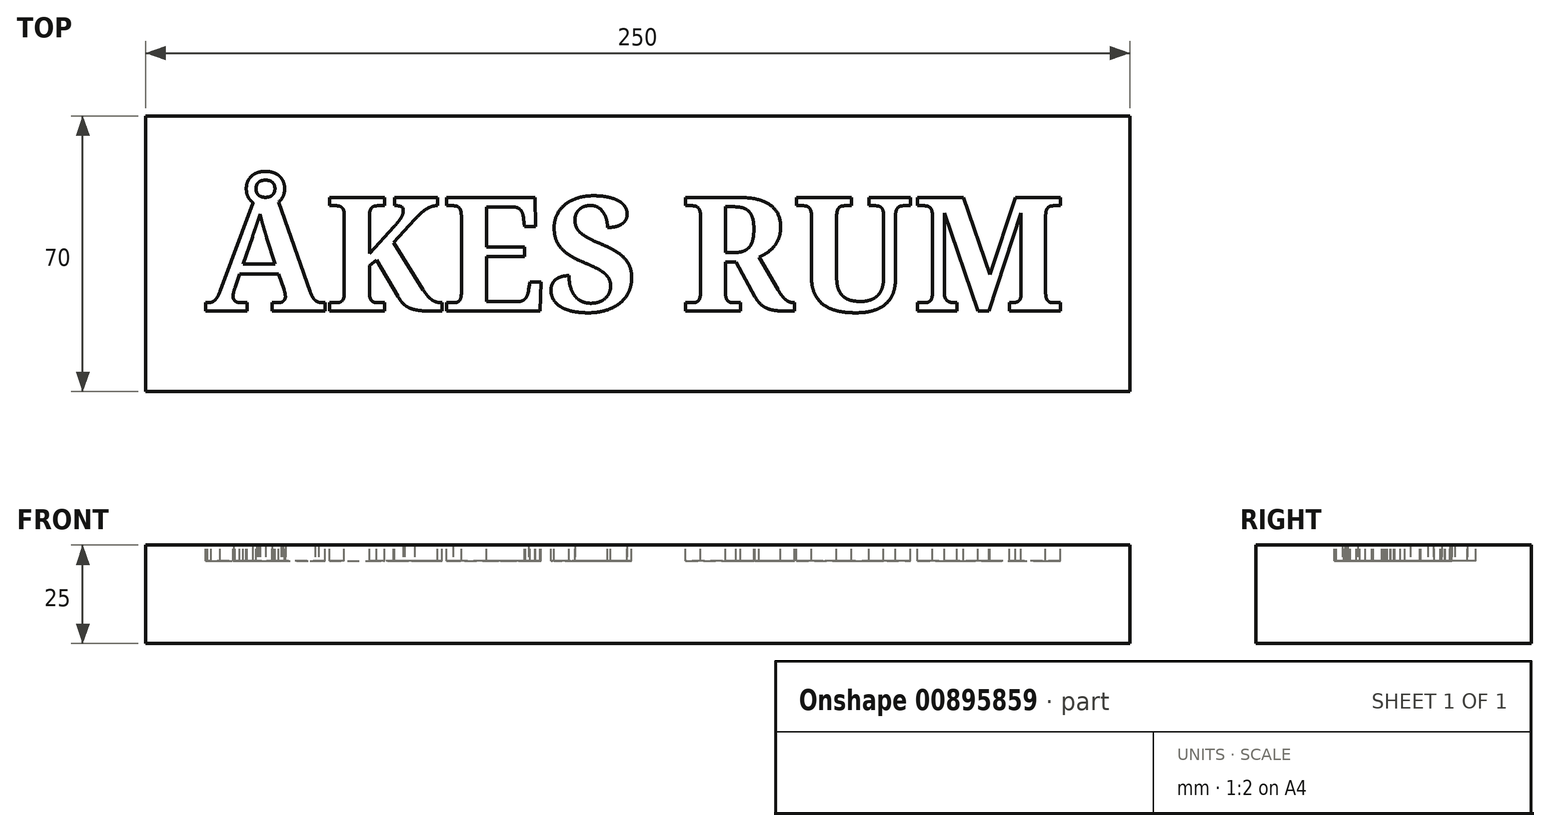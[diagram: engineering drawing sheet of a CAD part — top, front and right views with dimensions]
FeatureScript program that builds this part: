
annotation { "Feature Type Name" : "Feature", "Feature Type Description" : "" }
export const myFeature = defineFeature(function(context is Context, id is Id, definition is map)
    precondition{}
    {
        {
            var Q0;
            Q0=qCreatedBy(makeId("Top.planeOp"),FACE);
            var sketch = newSketch(context, id + "F0", { "sketchPlane" : qUnion([Q0])});
            skLineSegment(sketch, "E0.bottom", {"start": v(-344.85, -15.75) * mm, "end": v(-94.85, -15.75) * mm});
            skLineSegment(sketch, "E0.top", {"start": v(-344.85, -85.75) * mm, "end": v(-94.85, -85.75) * mm});
            skLineSegment(sketch, "E0.left", {"start": v(-344.85, -15.75) * mm, "end": v(-344.85, -85.75) * mm});
            skLineSegment(sketch, "E0.right", {"start": v(-94.85, -15.75) * mm, "end": v(-94.85, -85.75) * mm});
            skSolve(sketch);
        }
        {
            var Q0;
            Q0 = qSketchRegion(id + "F0", true);
            extrude(context, id + "F1", {"entities" : qUnion([Q0]), "depth" : 25 * mm, "offsetDistance" : 25 * mm});
        }
        {
            var Q0;
            Q0=makeQuery(id+"F1.opExtrude","CAP_FACE",FACE,{"disambiguationData":[OSD([sQuery(id+"F0.wireOp",EDGE,"E0.bottom"),sQuery(id+"F0.wireOp",EDGE,"E0.top"),sQuery(id+"F0.wireOp",EDGE,"E0.left"),sQuery(id+"F0.wireOp",EDGE,"E0.right")])],"isStart":false});
            var sketch = newSketch(context, id + "F2", { "sketchPlane" : qUnion([Q0])});
            skText(sketch, "E1", { "text": "ÅKES RUM", "fontName": "NotoSerif-Bold.ttf"});
            skLineSegment(sketch, "E2", {"start": v(-344.85, -50.75) * mm, "end": v(-94.85, -50.75) * mm, "construction": true});
            skLineSegment(sketch, "E3", {"start": v(-219.85, -15.75) * mm, "end": v(-219.85, -85.75) * mm, "construction": true});
            const initialGuessF2  = {"E1": [-0.32985, -0.06534, 1, 0, 0.02918]};
            skSetInitialGuess(sketch, initialGuessF2);
            skSolve(sketch);
        }
        {
            var Q0;
            Q0 = qSketchRegion(id + "F2", true);
            extrude(context, id + "F3", {"entities" : qUnion([Q0]), "operationType" : NewBodyOperationType.REMOVE, "oppositeDirection" : true, "depth" : 4 * mm, "offsetDistance" : 25 * mm});
        }
    });
